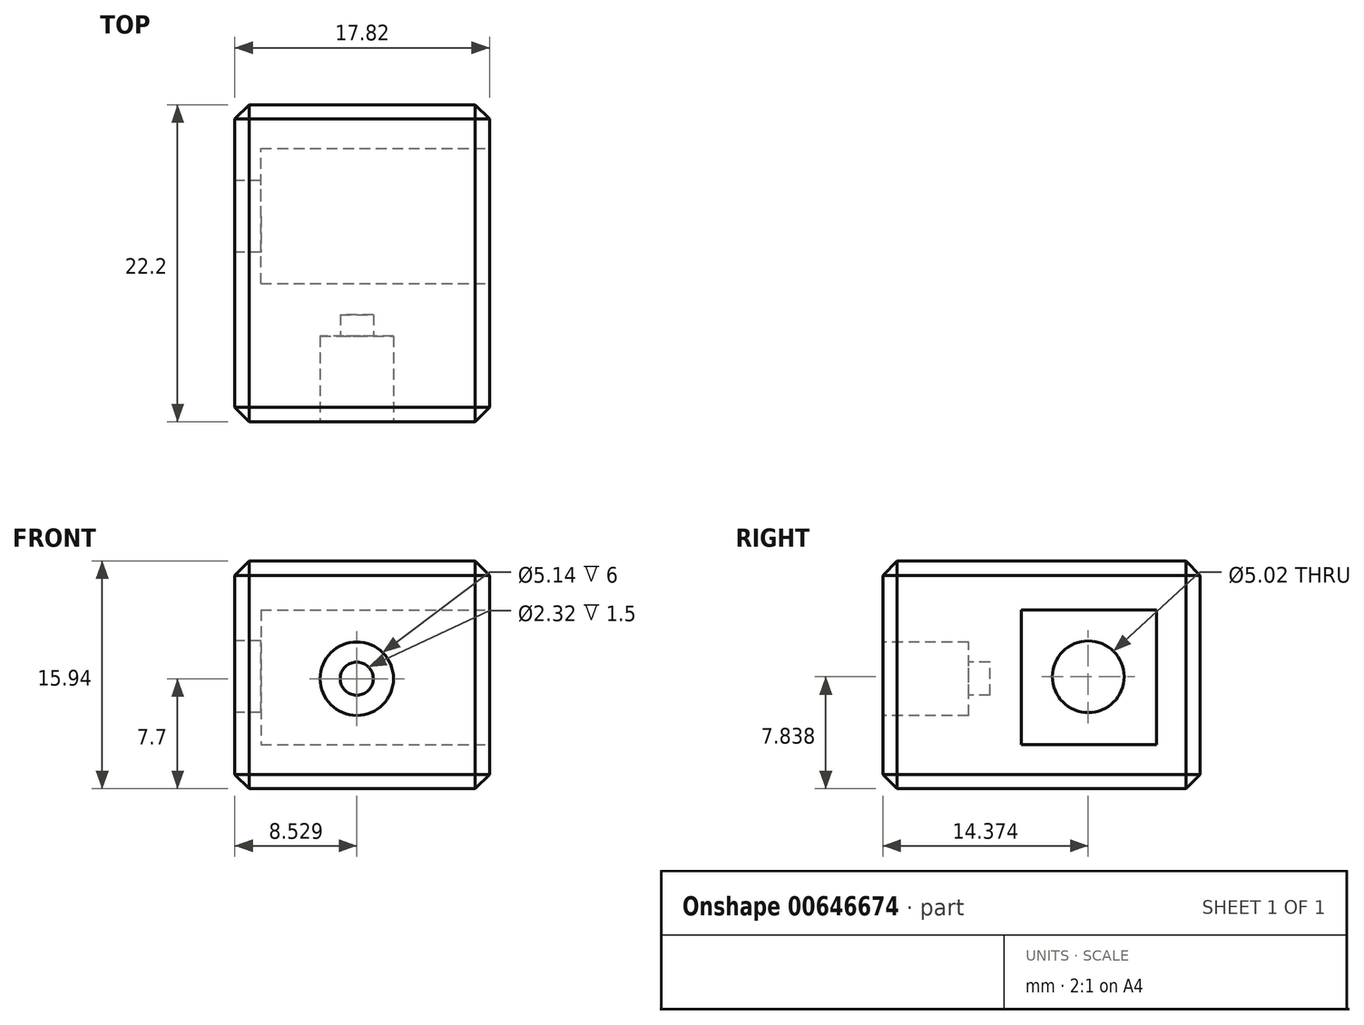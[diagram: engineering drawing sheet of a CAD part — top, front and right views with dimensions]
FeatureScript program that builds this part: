
annotation { "Feature Type Name" : "Feature", "Feature Type Description" : "" }
export const myFeature = defineFeature(function(context is Context, id is Id, definition is map)
    precondition{}
    {
        {
            var Q0;
            Q0=qCreatedBy(makeId("Front.planeOp"),FACE);
            var sketch = newSketch(context, id + "F0", { "sketchPlane" : qUnion([Q0])});
            skLineSegment(sketch, "E0.bottom", {"start": v(0, 0) * mm, "end": v(-17.82, 0) * mm});
            skLineSegment(sketch, "E0.top", {"start": v(0, 15.94) * mm, "end": v(-17.82, 15.94) * mm});
            skLineSegment(sketch, "E0.left", {"start": v(0, 0) * mm, "end": v(0, 15.94) * mm});
            skLineSegment(sketch, "E0.right", {"start": v(-17.82, 0) * mm, "end": v(-17.82, 15.94) * mm});
            skSolve(sketch);
        }
        {
            var Q0;
            Q0=makeQuery(id+"F0.imprint","IMPRINT",FACE,{"disambiguationData":[TD([[makeQuery(id+"F0.imprint","IMPRINT",EDGE,{"derivedFrom":sQuery(id+"F0.wireOp",EDGE,"E0.bottom")}),-1.0]])]});
            extrude(context, id + "F1", {"entities" : qUnion([Q0]), "depth" : 22.2 * mm, "offsetDistance" : 25 * mm});
        }
        {
            var Q0;
            Q0=makeQuery(id+"F1.opExtrude","CAP_FACE",FACE,{"disambiguationData":[OSD([sQuery(id+"F0.wireOp",EDGE,"E0.bottom"),sQuery(id+"F0.wireOp",EDGE,"E0.top"),sQuery(id+"F0.wireOp",EDGE,"E0.left"),sQuery(id+"F0.wireOp",EDGE,"E0.right")])],"isStart":false});
            var Q1;
            Q1=makeQuery(id+"F1.opExtrude","SWEPT_FACE",FACE,{"disambiguationData":[OSD([sQuery(id+"F0.wireOp",EDGE,"E0.left")])]});
            var Q2;
            Q2=makeQuery(id+"F1.opExtrude","SWEPT_FACE",FACE,{"disambiguationData":[OSD([sQuery(id+"F0.wireOp",EDGE,"E0.top")])]});
            var Q3;
            Q3=makeQuery(id+"F1.opExtrude","CAP_FACE",FACE,{"disambiguationData":[OSD([sQuery(id+"F0.wireOp",EDGE,"E0.bottom"),sQuery(id+"F0.wireOp",EDGE,"E0.top"),sQuery(id+"F0.wireOp",EDGE,"E0.left"),sQuery(id+"F0.wireOp",EDGE,"E0.right")])],"isStart":true});
            var Q4;
            Q4=makeQuery(id+"F1.opExtrude","SWEPT_FACE",FACE,{"disambiguationData":[OSD([sQuery(id+"F0.wireOp",EDGE,"E0.bottom")])]});
            var Q5;
            Q5=makeQuery(id+"F1.opExtrude","SWEPT_FACE",FACE,{"disambiguationData":[OSD([sQuery(id+"F0.wireOp",EDGE,"E0.right")])]});
            chamfer(context, id + "F2", {"entities" : qUnion([Q0, Q1, Q2, Q3, Q4, Q5]), "chamferType" : ChamferType.OFFSET_ANGLE, "width" : 1 * mm, "oppositeDirection" : true, "angle" : 45 * degree, "tangentPropagation" : true});
        }
        {
            var Q0;
            Q0=makeQuery(id+"F1.opExtrude","SWEPT_FACE",FACE,{"disambiguationData":[OSD([sQuery(id+"F0.wireOp",EDGE,"E0.left")])]});
            var sketch = newSketch(context, id + "F3", { "sketchPlane" : qUnion([Q0])});
            skLineSegment(sketch, "E1.bottom", {"start": v(-12.52, 12.5) * mm, "end": v(-3.04, 12.5) * mm});
            skLineSegment(sketch, "E1.top", {"start": v(-12.52, 3.08) * mm, "end": v(-3.04, 3.08) * mm});
            skLineSegment(sketch, "E1.left", {"start": v(-12.52, 12.5) * mm, "end": v(-12.52, 3.08) * mm});
            skLineSegment(sketch, "E1.right", {"start": v(-3.04, 12.5) * mm, "end": v(-3.04, 3.08) * mm});
            skPoint(sketch, "E1.middle", {"position": v(-7.78, 7.8) * mm});
            skSolve(sketch);
        }
        {
            var Q0;
            Q0=qSketchRegion(id+"F3",true);
            extrude(context, id + "F4", {"entities" : qUnion([Q0]), "operationType" : NewBodyOperationType.REMOVE, "oppositeDirection" : true, "depth" : 16 * mm, "offsetDistance" : 25 * mm});
        }
        {
            var Q0;
            Q0=makeQuery(id+"F1.opExtrude","SWEPT_FACE",FACE,{"disambiguationData":[OSD([sQuery(id+"F0.wireOp",EDGE,"E0.right")])]});
            var sketch = newSketch(context, id + "F5", { "sketchPlane" : qUnion([Q0])});
            skCircle(sketch, "E2", {"center": v(7.83, 7.84) * mm, "radius": 2.5 * mm});
            skSolve(sketch);
        }
        {
            var Q0;
            Q0=qSketchRegion(id+"F5",true);
            extrude(context, id + "F6", {"entities" : qUnion([Q0]), "operationType" : NewBodyOperationType.REMOVE, "oppositeDirection" : true, "depth" : 25 * mm, "offsetDistance" : 25 * mm});
        }
        {
            var Q0;
            Q0=makeQuery(id+"F1.opExtrude","CAP_FACE",FACE,{"disambiguationData":[OSD([sQuery(id+"F0.wireOp",EDGE,"E0.bottom"),sQuery(id+"F0.wireOp",EDGE,"E0.top"),sQuery(id+"F0.wireOp",EDGE,"E0.left"),sQuery(id+"F0.wireOp",EDGE,"E0.right")])],"isStart":false});
            var sketch = newSketch(context, id + "F7", { "sketchPlane" : qUnion([Q0])});
            skCircle(sketch, "E3", {"center": v(-9.3, 7.7) * mm, "radius": 2.57 * mm});
            skSolve(sketch);
        }
        {
            var Q0;
            Q0=makeQuery(id+"F7.imprint","IMPRINT",FACE,{"disambiguationData":[TD([[makeQuery(id+"F7.imprint","IMPRINT",EDGE,{"derivedFrom":sQuery(id+"F7.wireOp",EDGE,"E3")}),1.0]])]});
            extrude(context, id + "F8", {"entities" : qUnion([Q0]), "operationType" : NewBodyOperationType.REMOVE, "oppositeDirection" : true, "depth" : 6 * mm, "offsetDistance" : 25 * mm});
        }
        {
            var Q0;
            Q0=makeQuery(id+"F8.boolean.opBoolean","COPY",FACE,{"derivedFrom":makeQuery(id+"F8.opExtrude","CAP_FACE",FACE,{"disambiguationData":[OSD([sQuery(id+"F7.wireOp",EDGE,"E3")])],"isStart":false})});
            var sketch = newSketch(context, id + "F9", { "sketchPlane" : qUnion([Q0])});
            skCircle(sketch, "E4", {"center": v(-9.3, 7.7) * mm, "radius": 1.16 * mm});
            skSolve(sketch);
        }
        {
            var Q0;
            Q0 = qSketchRegion(id + "F9", true);
            extrude(context, id + "F10", {"entities" : qUnion([Q0]), "operationType" : NewBodyOperationType.REMOVE, "oppositeDirection" : true, "depth" : 1.5 * mm, "offsetDistance" : 25 * mm});
        }
    });
